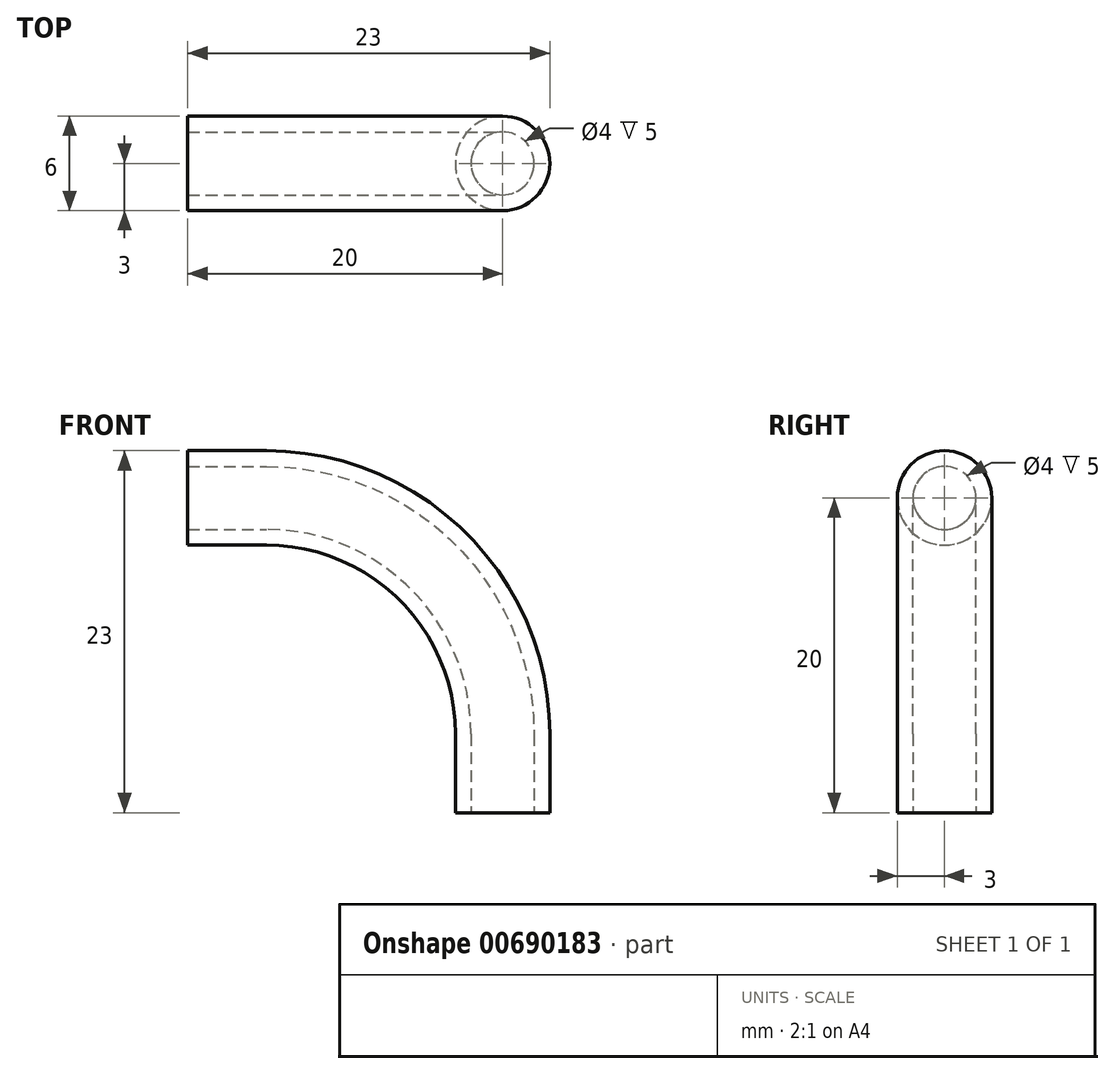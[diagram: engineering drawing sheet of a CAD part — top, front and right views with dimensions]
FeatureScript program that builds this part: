
annotation { "Feature Type Name" : "Feature", "Feature Type Description" : "" }
export const myFeature = defineFeature(function(context is Context, id is Id, definition is map)
    precondition{}
    {
        {
            var Q0;
            Q0=qCreatedBy(makeId("Front.planeOp"),FACE);
            var sketch = newSketch(context, id + "F0", { "sketchPlane" : qUnion([Q0])});
            skArc(sketch, "E0", {"start": v(0, 0) * mm, "mid": v(-4.4, 10.6) * mm, "end": v(-15, 15) * mm});
            skLineSegment(sketch, "E1", {"start": v(-15, 15) * mm, "end": v(-20, 15) * mm});
            skLineSegment(sketch, "E2", {"start": v(0, 0) * mm, "end": v(0, -5) * mm});
            skSolve(sketch);
        }
        {
            var Q0;
            Q0=qCreatedBy(makeId("Top.planeOp"),FACE);
            var sketch = newSketch(context, id + "F1", { "sketchPlane" : qUnion([Q0])});
            skCircle(sketch, "E3", {"center": v(0, 0) * mm, "radius": 2 * mm});
            skCircle(sketch, "E4", {"center": v(0, 0) * mm, "radius": 3 * mm});
            skSolve(sketch);
        }
        {
            var Q0;
            Q0=qSketchRegion(id+"F1",true);
            var Q1;
            Q1=qConstructionFilter(qBodyType(qCreatedBy(id+"F0",EDGE),BodyType.WIRE),ConstructionObject.NO);
            sweep(context, id + "F2", {"profiles" : qUnion([Q0]), "path" : qUnion([Q1])});
        }
    });
